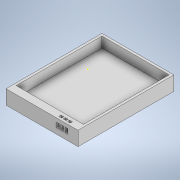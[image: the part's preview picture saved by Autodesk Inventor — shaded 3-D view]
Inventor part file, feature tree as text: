
AUTODESK INVENTOR PART (.ipt)
format: ipt  version: 2021 (Build 250183000, 183)  size: 263,680 bytes
history: native  units: in
note: dims shown in document units (in); Inventor stores cm internally (conversion verified against a paired STEP export)
features: sketch x11, extrude x10
ambient origin geometry x8: Origin, YZ Plane, XZ Plane, XY Plane, X Axis, Y Axis, Z Axis, Center Point
bodies: Solid1 (feature_tree)
feature tree (21):
  extrude  "Extrusion1"  Depth=1.315in
  extrude  "Extrusion2"  Depth=0.0433in
  extrude  "Extrusion3"  Depth=0.0433in
  extrude  "Extrusion4"  Depth=1.5669in
  sketch  "Sketch6"  dims[d11=0.1929in d12=0.0in d13=0.0236in d14=0.0in]
  extrude  "Extrusion5"  Depth=0.0236in TaperAngle=0.0deg
  extrude  "Extrusion6"  Depth=0.1181in
  sketch  "Sketch8"  dims[d18=0.0512in d19=0.1417in]
  extrude  "Extrusion7"  Depth=0.1417in
  extrude  "Extrusion8"  Depth=0.0984in TaperAngle=0.0deg
  extrude  "Extrusion9"  Depth=0.1181in
  extrude  "Extrusion10"  Depth=0.0276in
  sketch  "Sketch2"  dims[d2=1.6535in d3=1.315in]
  sketch  "Sketch3"  dims[d4=0.2362in d5=0.0in d6=0.0433in]
  sketch  "Sketch4"  dims[d7=0.0433in d8=0.0433in]
  sketch  "Sketch5"  dims[d9=0.0433in d10=1.5669in]
  sketch  "Sketch7"  dims[d15=0.1181in d16=0.0in d17=0.1181in]
  sketch  "Sketch9"  dims[d20=0.0394in d21=0.0984in d22=0.0in]
  sketch  "Sketch10"  dims[d23=0.1181in d24=0.0512in d25=0.1181in d26=0.0512in d27=0.0394in]
  sketch  "Sketch11"  dims[d28=0.0394in d29=0.0276in]
  sketch  "Sketch12"  dims[d30=0.0276in d31=0.0in d32=0.0in d33=0.0118in d34=0.0787in d35=0.0118in d36=0.0512in d37=0.0in d38=0.0792in d39=0.0118in d40=0.0512in d41=0.0in d42=0.0787in d43=0.0984in d44=0.0in d45=0.0512in d46=0.0394in d47=0.0in d48=0.0591in d49=0.0512in d50=0.0394in d51=0.0512in d52=0.0394in d53=0.0591in d54=0.0591in d55=0.0in d56=0.0in d57=0.0591in d58=0.0in d59=0.0315in d60=0.0591in d61=0.0in d62=0.0433in d63=0.0in d64=0.0in]
